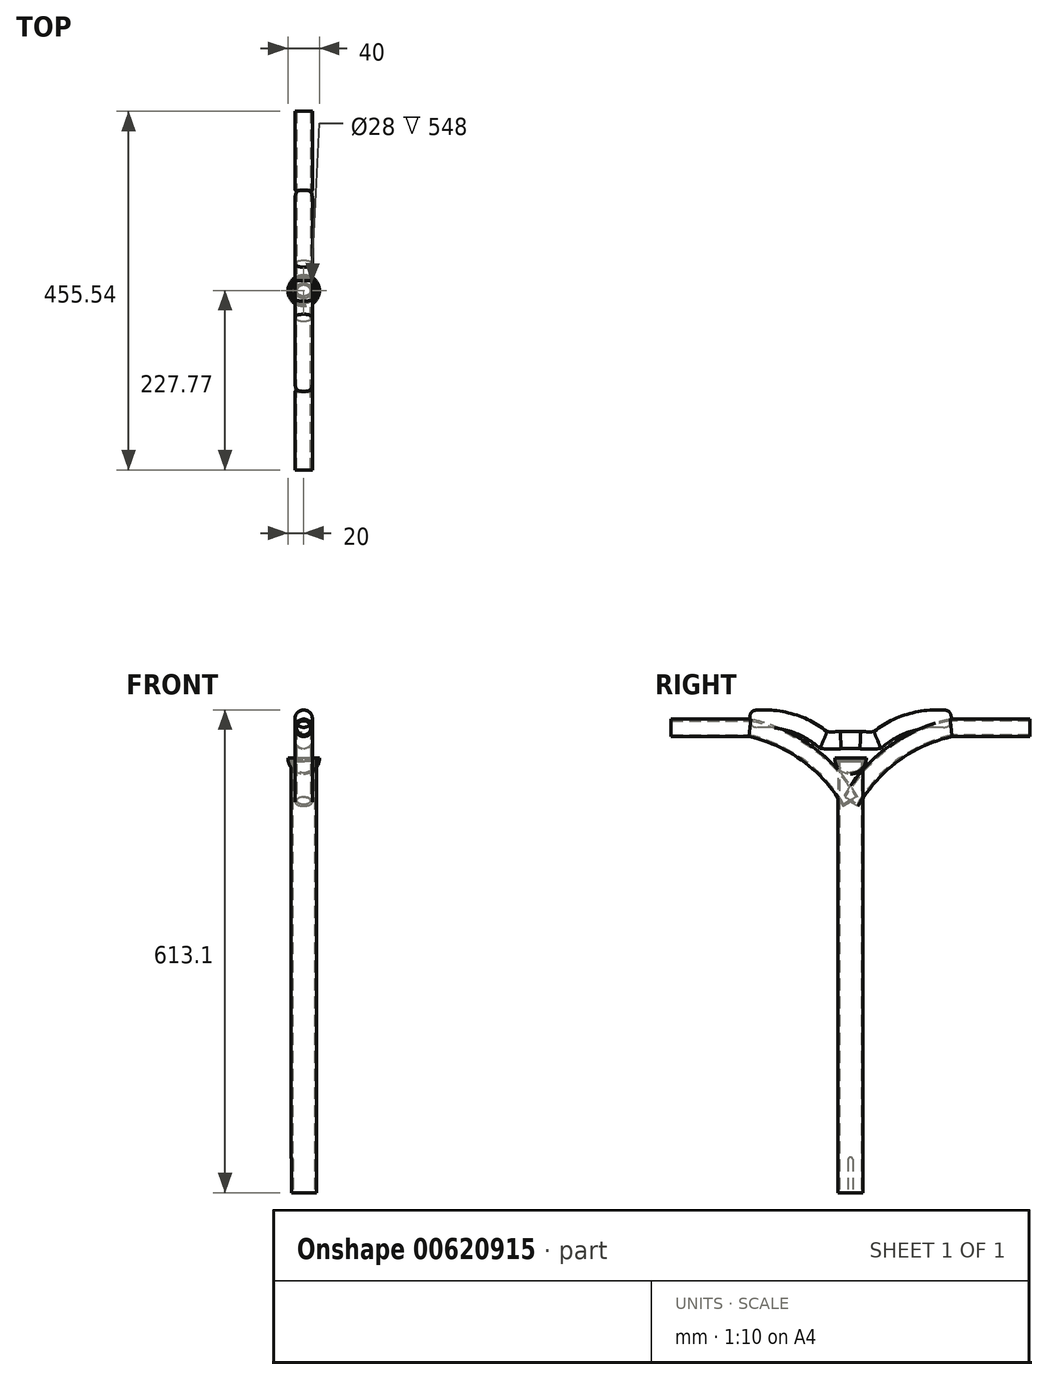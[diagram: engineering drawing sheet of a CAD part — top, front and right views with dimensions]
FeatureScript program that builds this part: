
annotation { "Feature Type Name" : "Feature", "Feature Type Description" : "" }
export const myFeature = defineFeature(function(context is Context, id is Id, definition is map)
    precondition{}
    {
        {
            var Q0;
            Q0=qCreatedBy(makeId("Top.planeOp"),FACE);
            var sketch = newSketch(context, id + "F0", { "sketchPlane" : qUnion([Q0])});
            skCircle(sketch, "E0", {"center": v(0, 0) * mm, "radius": 16 * mm});
            skSolve(sketch);
        }
        {
            var Q0;
            Q0=qSketchRegion(id+"F0",true);
            extrude(context, id + "F1", {"entities" : qUnion([Q0]), "depth" : 550 * mm});
        }
        {
            var Q0;
            Q0=makeQuery(id+"F1.opExtrude","CAP_FACE",FACE,{"disambiguationData":[OSD([sQuery(id+"F0.wireOp",EDGE,"E0")])],"isStart":true});
            shell(context, id + "F2", {"entities" : qUnion([Q0]), "thickness" : 2 * mm});
        }
        {
            var Q0;
            Q0=qCreatedBy(makeId("Right.planeOp"),FACE);
            var sketch = newSketch(context, id + "F3", { "sketchPlane" : qUnion([Q0])});
            skLineSegment(sketch, "E1.bottom", {"start": v(3, 0) * mm, "end": v(-3, 0) * mm});
            skLineSegment(sketch, "E1.top", {"start": v(0, 45) * mm, "end": v(0, 45) * mm});
            skLineSegment(sketch, "E1.left", {"start": v(3, 0) * mm, "end": v(3, 42) * mm});
            skLineSegment(sketch, "E1.right", {"start": v(-3, 0) * mm, "end": v(-3, 42) * mm});
            skPoint(sketch, "E2", {"position": v(0, 45) * mm});
            skPoint(sketch, "E3.visualSharp", {"position": v(3, 45) * mm});
            skArc(sketch, "E3.filletArc", {"start": v(3, 42) * mm, "mid": v(2.12, 44.12) * mm, "end": v(0, 45) * mm});
            skPoint(sketch, "E4.visualSharp", {"position": v(-3, 45) * mm});
            skArc(sketch, "E4.filletArc", {"start": v(0, 45) * mm, "mid": v(-2.12, 44.12) * mm, "end": v(-3, 42) * mm});
            skSolve(sketch);
        }
        {
            var Q0;
            Q0=qSketchRegion(id+"F3",true);
            extrude(context, id + "F4", {"entities" : qUnion([Q0]), "operationType" : NewBodyOperationType.REMOVE, "endBound" : BoundingType.THROUGH_ALL, "oppositeDirection" : true, "depth" : 25 * mm});
        }
        {
            var Q0;
            Q0=qCreatedBy(makeId("Right.planeOp"),FACE);
            var sketch = newSketch(context, id + "F5", { "sketchPlane" : qUnion([Q0])});
            skArc(sketch, "E5", {"start": v(127.77, 590.48) * mm, "mid": v(53.89, 557.03) * mm, "end": v(0, 496.4) * mm});
            skLineSegment(sketch, "E6", {"start": v(127.77, 590.48) * mm, "end": v(227.77, 590.48) * mm});
            skSolve(sketch);
        }
        {
            var Q0;
            Q0=sQuery(id+"F5.wireOp",VERTEX,"E6.end");
            var Q1;
            Q1=qCreatedBy(makeId("Front.planeOp"),FACE);
            cPlane(context, id + "F6", {"entities" : qUnion([Q0, Q1]), "cplaneType" : CPlaneType.PLANE_POINT, "offset" : 150 * mm, "width" : 150 * mm, "height" : 150 * mm});
        }
        {
            var Q0;
            Q0=qCreatedBy(id+"F6.planeOp",FACE);
            var sketch = newSketch(context, id + "F7", { "sketchPlane" : qUnion([Q0])});
            skCircle(sketch, "E7", {"center": v(0, 590.48) * mm, "radius": 11 * mm});
            skSolve(sketch);
        }
        {
            var Q0;
            Q0=qSketchRegion(id+"F7",true);
            var Q1;
            Q1=qConstructionFilter(qBodyType(qCreatedBy(id+"F5",EDGE),BodyType.WIRE),ConstructionObject.NO);
            sweep(context, id + "F8", {"profiles" : qUnion([Q0]), "path" : qUnion([Q1])});
        }
        {
            var Q0;
            Q0=makeQuery(id+"F8.opSweep","CAP_FACE",FACE,{"disambiguationData":[OSD([sQuery(id+"F5.wireOp",VERTEX,"E6.end"),sQuery(id+"F7.wireOp",EDGE,"E7")])],"isStart":true});
            shell(context, id + "F9", {"entities" : qUnion([Q0]), "thickness" : 2 * mm});
        }
        {
            var Q0;
            Q0=makeQuery(id+"F8.opSweep","SWEPT_BODY",BODY,{"disambiguationData":[OSD([sQuery(id+"F5.wireOp",EDGE,"E6"),sQuery(id+"F7.wireOp",EDGE,"E7")])]});
            var Q1;
            Q1=qCreatedBy(makeId("Front.planeOp"),FACE);
            mirror(context, id + "F10", {"entities" : qUnion([Q0]), "mirrorPlane" : qUnion([Q1])});
        }
        {
            var Q0;
            Q0=qCreatedBy(makeId("Right.planeOp"),FACE);
            var sketch = newSketch(context, id + "F11", { "sketchPlane" : qUnion([Q0])});
            skLineSegment(sketch, "E8", {"start": v(-128, 602.1) * mm, "end": v(-108, 602.1) * mm});
            skArc(sketch, "E9", {"start": v(-34.22, 575) * mm, "mid": v(-68.7, 595.11) * mm, "end": v(-108, 602.1) * mm});
            skArc(sketch, "E10", {"start": v(-34.22, 575) * mm, "mid": v(-23.36, 574.47) * mm, "end": v(-12.5, 575) * mm});
            skLineSegment(sketch, "E11", {"start": v(-12.5, 575) * mm, "end": v(0, 575) * mm});
            skLineSegment(sketch, "E12", {"start": v(0, 0) * mm, "end": v(0, 576.94) * mm, "construction": true});
            skLineSegment(sketch, "E13.MirrorCS", {"start": v(128, 602.1) * mm, "end": v(108, 602.1) * mm});
            skArc(sketch, "E14.MirrorCS", {"start": v(34.22, 575) * mm, "mid": v(68.7, 595.11) * mm, "end": v(108, 602.1) * mm});
            skArc(sketch, "E15.MirrorCS", {"start": v(34.22, 575) * mm, "mid": v(23.36, 574.47) * mm, "end": v(12.5, 575) * mm});
            skLineSegment(sketch, "E16.MirrorCS", {"start": v(12.5, 575) * mm, "end": v(0, 575) * mm});
            skSolve(sketch);
        }
        {
            var Q0;
            Q0=sQuery(id+"F11.wireOp",VERTEX,"E13.MirrorCS.start");
            var Q1;
            Q1=qCreatedBy(id+"F6.planeOp",FACE);
            cPlane(context, id + "F12", {"entities" : qUnion([Q0, Q1]), "cplaneType" : CPlaneType.PLANE_POINT, "offset" : 150 * mm, "width" : 150 * mm, "height" : 150 * mm});
        }
        {
            var Q0;
            Q0=qCreatedBy(id+"F12.planeOp",FACE);
            var sketch = newSketch(context, id + "F13", { "sketchPlane" : qUnion([Q0])});
            skCircle(sketch, "E17", {"center": v(0, 602.1) * mm, "radius": 11 * mm});
            skSolve(sketch);
        }
        {
            var Q0;
            Q0=qSketchRegion(id+"F13",true);
            var Q1;
            Q1=sQuery(id+"F11.wireOp",EDGE,"E8");
            var Q2;
            Q2=sQuery(id+"F11.wireOp",EDGE,"E9");
            var Q3;
            Q3=sQuery(id+"F11.wireOp",EDGE,"E10");
            var Q4;
            Q4=sQuery(id+"F11.wireOp",EDGE,"E11");
            var Q5;
            Q5=sQuery(id+"F11.wireOp",EDGE,"E16.MirrorCS");
            var Q6;
            Q6=sQuery(id+"F11.wireOp",EDGE,"E15.MirrorCS");
            var Q7;
            Q7=sQuery(id+"F11.wireOp",EDGE,"E14.MirrorCS");
            var Q8;
            Q8=sQuery(id+"F11.wireOp",EDGE,"E13.MirrorCS");
            sweep(context, id + "F14", {"profiles" : qUnion([Q0]), "path" : qUnion([Q1, Q2, Q3, Q4, Q5, Q6, Q7, Q8])});
        }
        {
            var Q0;
            {var subQ0=sQuery(id+"F13.wireOp",EDGE,"E17");var subQ1=sQuery(id+"F11.wireOp",VERTEX,"E13.MirrorCS.start");Q0=makeQuery(id+"F14.boolean.opBoolean","SPLIT",EDGE,{"disambiguationData":[TD([makeQuery(id+"F8.opSweep","SWEPT_FACE",FACE,{"disambiguationData":[OSD([sQuery(id+"F5.wireOp",EDGE,"E6"),sQuery(id+"F7.wireOp",EDGE,"E7")])]})])],"derivedFrom":makeQuery(id+"F14.opSweep","CAP_EDGE",EDGE,{"disambiguationData":[OSD([subQ1,subQ0])],"isStart":true})});}
            var Q1;
            {var subQ0=sQuery(id+"F13.wireOp",EDGE,"E17");var subQ1=sQuery(id+"F11.wireOp",VERTEX,"E8.start");Q1=makeQuery(id+"F14.boolean.opBoolean","SPLIT",EDGE,{"disambiguationData":[TD([makeQuery(id+"F10.opPattern","COPY",FACE,{"derivedFrom":makeQuery(id+"F8.opSweep","SWEPT_FACE",FACE,{"disambiguationData":[OSD([sQuery(id+"F5.wireOp",EDGE,"E6"),sQuery(id+"F7.wireOp",EDGE,"E7")])]}),"instanceName":"1"})])],"derivedFrom":makeQuery(id+"F14.opSweep","CAP_EDGE",EDGE,{"disambiguationData":[OSD([subQ1,subQ0])],"isStart":false})});}
            fillet(context, id + "F15", {"entities" : qUnion([Q0, Q1]), "radius" : 10 * mm, "tangentPropagation" : true, "rho" : 0.5, "crossSection" : FilletCrossSection.CONIC, "allowEdgeOverflow" : false});
        }
        {
            var Q0;
            Q0=qCreatedBy(makeId("Right.planeOp"),FACE);
            var sketch = newSketch(context, id + "F16", { "sketchPlane" : qUnion([Q0])});
            skArc(sketch, "E18", {"start": v(0, 532) * mm, "mid": v(14.14, 537.86) * mm, "end": v(20, 552) * mm});
            skLineSegment(sketch, "E19", {"start": v(0, 532) * mm, "end": v(0, 552) * mm});
            skLineSegment(sketch, "E20", {"start": v(20, 552) * mm, "end": v(0, 552) * mm});
            skSolve(sketch);
        }
        {
            var Q0;
            Q0=makeQuery(id+"F16.imprint","IMPRINT",FACE,{"disambiguationData":[TD([[makeQuery(id+"F16.imprint","IMPRINT",EDGE,{"derivedFrom":sQuery(id+"F16.wireOp",EDGE,"E18")}),1.0]])]});
            var Q1;
            Q1=sQuery(id+"F16.wireOp",EDGE,"E19");
            revolve(context, id + "F17", {"entities" : qUnion([Q0]), "axis" : qUnion([Q1]), "revolveType" : RevolveType.FULL});
        }
        {
            var Q0;
            Q0=makeQuery(id+"F17.opRevolve","SWEPT_FACE",FACE,{"disambiguationData":[OSD([sQuery(id+"F16.wireOp",EDGE,"E20")])]});
            shell(context, id + "F18", {"entities" : qUnion([Q0]), "thickness" : 2 * mm});
        }
    });
